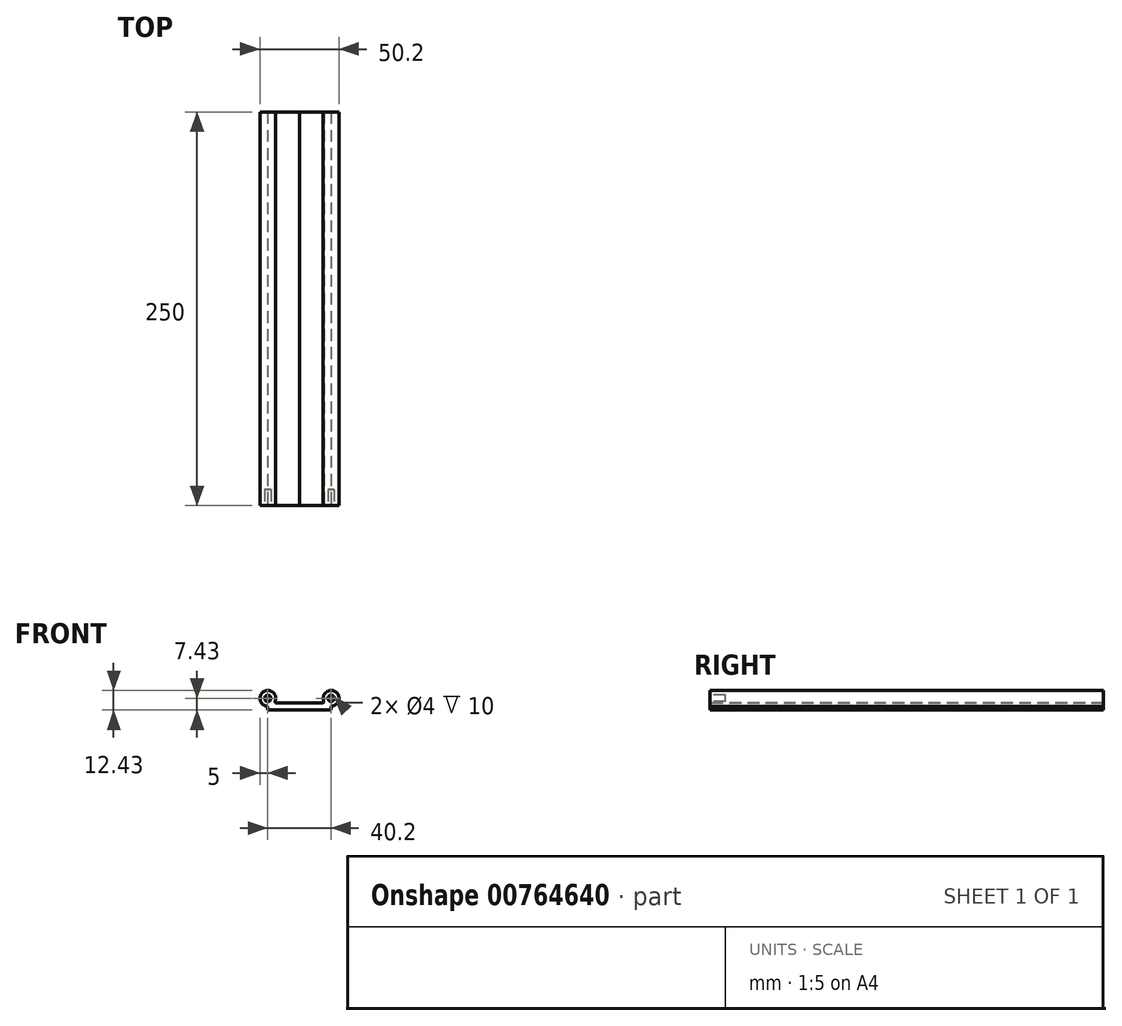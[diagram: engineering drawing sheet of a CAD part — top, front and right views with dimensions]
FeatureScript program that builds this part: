
annotation { "Feature Type Name" : "Feature", "Feature Type Description" : "" }
export const myFeature = defineFeature(function(context is Context, id is Id, definition is map)
    precondition{}
    {
        {
            var Q0;
            Q0=qCreatedBy(makeId("Front.planeOp"),FACE);
            var sketch = newSketch(context, id + "F0", { "sketchPlane" : qUnion([Q0])});
            skArc(sketch, "E0", {"start": v(-15.4, -1.72) * mm, "mid": v(-22.96, 4.1) * mm, "end": v(-20.1, -5) * mm});
            skArc(sketch, "E1", {"start": v(20.1, -5) * mm, "mid": v(22.96, 4.1) * mm, "end": v(15.4, -1.72) * mm});
            skLineSegment(sketch, "E2.bottom", {"start": v(-14.46, -3.06) * mm, "end": v(-0.1, -3.06) * mm});
            skLineSegment(sketch, "E2.top", {"start": v(-20.1, -7.43) * mm, "end": v(20.1, -7.43) * mm});
            skLineSegment(sketch, "E2.left", {"start": v(-20.1, -5) * mm, "end": v(-20.1, -7.43) * mm});
            skLineSegment(sketch, "E2.right", {"start": v(20.1, -5) * mm, "end": v(20.1, -7.43) * mm});
            skPoint(sketch, "E3.visualSharp", {"position": v(-16.15, -3.06) * mm});
            skArc(sketch, "E3.filletArc", {"start": v(-15.4, -1.72) * mm, "mid": v(-15.28, -2.63) * mm, "end": v(-14.46, -3.06) * mm});
            skPoint(sketch, "E4.visualSharp", {"position": v(16.15, -3.06) * mm});
            skArc(sketch, "E4.filletArc", {"start": v(14.46, -3.06) * mm, "mid": v(15.28, -2.63) * mm, "end": v(15.4, -1.72) * mm});
            skLineSegment(sketch, "E5", {"start": v(-0.1, -3.06) * mm, "end": v(0, -3.16) * mm});
            skPoint(sketch, "E5.endSnap0", {"position": v(0, -3.06) * mm});
            skLineSegment(sketch, "E6", {"start": v(0, -3.16) * mm, "end": v(0.1, -3.06) * mm});
            skLineSegment(sketch, "E7.trimOffspring", {"start": v(0.1, -3.06) * mm, "end": v(14.46, -3.06) * mm});
            skSolve(sketch);
        }
        {
            var Q0;
            Q0=makeQuery(id+"F0.imprint","IMPRINT",FACE,{"disambiguationData":[TD([[makeQuery(id+"F0.imprint","IMPRINT",EDGE,{"derivedFrom":sQuery(id+"F0.wireOp",EDGE,"E0")}),1.0]])]});
            extrude(context, id + "F1", {"entities" : qUnion([Q0]), "oppositeDirection" : true, "depth" : 250 * mm, "offsetDistance" : 25 * mm});
        }
        {
            var Q0;
            Q0=makeQuery(id+"F1.opExtrude","CAP_FACE",FACE,{"disambiguationData":[OSD([sQuery(id+"F0.wireOp",EDGE,"E0"),sQuery(id+"F0.wireOp",EDGE,"E1"),sQuery(id+"F0.wireOp",EDGE,"E2.bottom"),sQuery(id+"F0.wireOp",EDGE,"E2.top"),sQuery(id+"F0.wireOp",EDGE,"E2.left"),sQuery(id+"F0.wireOp",EDGE,"E2.right"),sQuery(id+"F0.wireOp",EDGE,"E3.filletArc"),sQuery(id+"F0.wireOp",EDGE,"E4.filletArc"),sQuery(id+"F0.wireOp",EDGE,"E5"),sQuery(id+"F0.wireOp",EDGE,"E6"),sQuery(id+"F0.wireOp",EDGE,"E7.trimOffspring")])],"isStart":true});
            var sketch = newSketch(context, id + "F2", { "sketchPlane" : qUnion([Q0])});
            skCircle(sketch, "E8", {"center": v(-20.1, 0) * mm, "radius": 2 * mm});
            skCircle(sketch, "E9", {"center": v(20.1, 0) * mm, "radius": 2 * mm});
            skSolve(sketch);
        }
        {
            var Q0;
            Q0 = qSketchRegion(id + "F2", true);
            extrude(context, id + "F3", {"entities" : qUnion([Q0]), "operationType" : NewBodyOperationType.REMOVE, "oppositeDirection" : true, "depth" : 10 * mm, "offsetDistance" : 25 * mm});
        }
    });
